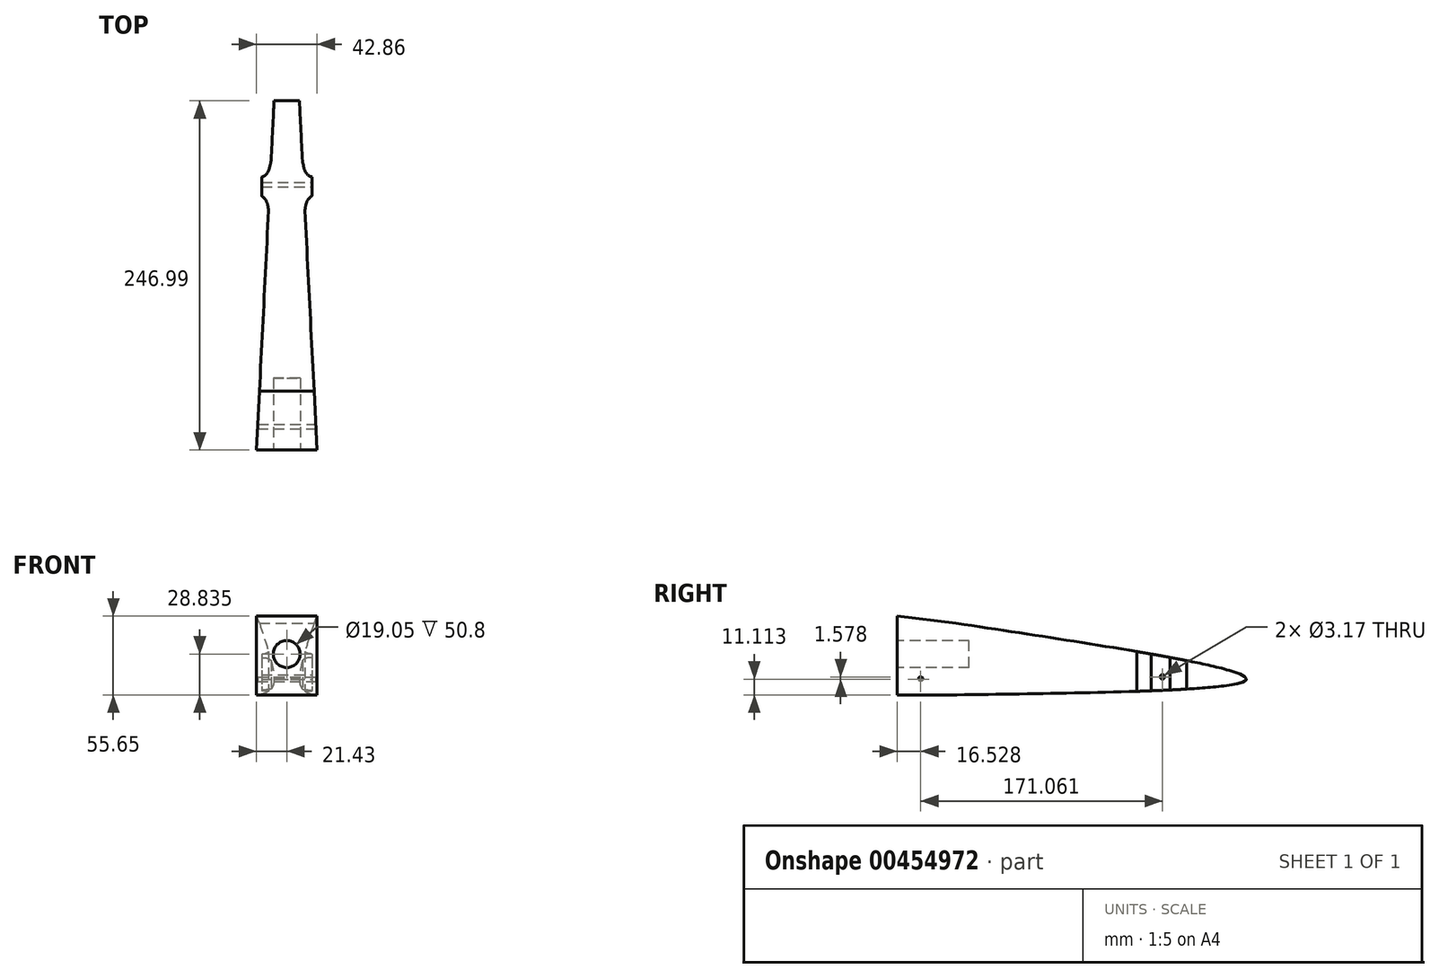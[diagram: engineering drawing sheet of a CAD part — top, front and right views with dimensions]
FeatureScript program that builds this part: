
annotation { "Feature Type Name" : "Feature", "Feature Type Description" : "" }
export const myFeature = defineFeature(function(context is Context, id is Id, definition is map)
    precondition{}
    {
        {
            var Q0;
            Q0=qCreatedBy(makeId("Right.planeOp"),FACE);
            var sketch = newSketch(context, id + "F0", { "sketchPlane" : qUnion([Q0])});
            skLineSegment(sketch, "E0", {"start": v(-152.4, 0) * mm, "end": v(152.4, 0) * mm});
            skLineSegment(sketch, "E1", {"start": v(-152.4, 0) * mm, "end": v(-152.4, 69.85) * mm});
            skLineSegment(sketch, "E2", {"start": v(152.4, 0) * mm, "end": v(152.4, 19.05) * mm});
            skLineSegment(sketch, "E3", {"start": v(152.4, 19.05) * mm, "end": v(-152.4, 69.85) * mm});
            skPoint(sketch, "E4.endSnap0", {"position": v(-152.4, 34.93) * mm});
            skLineSegment(sketch, "E5.0", {"start": v(-95.25, 50.8) * mm, "end": v(-152.4, 50.8) * mm, "construction": true});
            skLineSegment(sketch, "E5.1", {"start": v(-95.25, 50.8) * mm, "end": v(-95.25, 19.05) * mm, "construction": true});
            skLineSegment(sketch, "E5.2", {"start": v(-95.25, 19.05) * mm, "end": v(-152.4, 19.05) * mm, "construction": true});
            skSolve(sketch);
        }
        {
            var Q0;
            Q0=makeQuery(id+"F0.imprint","IMPRINT",FACE,{"disambiguationData":[TD([[makeQuery(id+"F0.imprint","IMPRINT",EDGE,{"derivedFrom":sQuery(id+"F0.wireOp",EDGE,"E0")}),1.0]])]});
            extrude(context, id + "F1", {"entities" : qUnion([Q0]), "depth" : 42.86 * mm, "symmetric" : true});
        }
        {
            var Q0;
            Q0=makeQuery(id+"F1.opExtrude","SWEPT_FACE",FACE,{"disambiguationData":[OSD([sQuery(id+"F0.wireOp",EDGE,"E1")])]});
            var sketch = newSketch(context, id + "F2", { "sketchPlane" : qUnion([Q0])});
            skLineSegment(sketch, "E6", {"start": v(21.43, 34.93) * mm, "end": v(0, 34.93) * mm, "construction": true});
            skCircle(sketch, "E7", {"center": v(0, 34.93) * mm, "radius": 9.53 * mm});
            skSolve(sketch);
        }
        {
            var Q0;
            Q0=makeQuery(id+"F2.imprint","IMPRINT",FACE,{"disambiguationData":[TD([[makeQuery(id+"F2.imprint","IMPRINT",EDGE,{"derivedFrom":sQuery(id+"F2.wireOp",EDGE,"E7")}),1.0]])]});
            var Q1;
            Q1=sQuery(id+"F2.wireOp",EDGE,"E7");
            extrude(context, id + "F3", {"entities" : qUnion([Q0]), "operationType" : NewBodyOperationType.REMOVE, "surfaceEntities" : qUnion([Q1]), "oppositeDirection" : true, "depth" : 50.8 * mm});
        }
        {
            var Q0;
            Q0=makeQuery(id+"F1.opExtrude","CAP_FACE",FACE,{"disambiguationData":[OSD([sQuery(id+"F0.wireOp",EDGE,"E0"),sQuery(id+"F0.wireOp",EDGE,"E1"),sQuery(id+"F0.wireOp",EDGE,"E2"),sQuery(id+"F0.wireOp",EDGE,"E3")])],"isStart":false});
            var sketch = newSketch(context, id + "F4", { "sketchPlane" : qUnion([Q0])});
            skLineSegment(sketch, "E8", {"start": v(-152.4, 34.93) * mm, "end": v(-152.4, 44.45) * mm, "construction": true});
            skLineSegment(sketch, "E9.0", {"start": v(-95.25, 19.05) * mm, "end": v(-152.4, 19.05) * mm, "construction": true});
            skLineSegment(sketch, "E9.1", {"start": v(-95.25, 50.8) * mm, "end": v(-95.25, 19.05) * mm, "construction": true});
            skLineSegment(sketch, "E9.2", {"start": v(-152.4, 50.8) * mm, "end": v(-95.25, 50.8) * mm, "construction": true});
            skLineSegment(sketch, "E10", {"start": v(57.15, 0) * mm, "end": v(57.15, 34.93) * mm, "construction": true});
            skLineSegment(sketch, "E11", {"start": v(-152.4, 44.45) * mm, "end": v(-101.6, 44.45) * mm, "construction": true});
            skLineSegment(sketch, "E12", {"start": v(-101.6, 44.45) * mm, "end": v(-101.6, 25.4) * mm, "construction": true});
            skLineSegment(sketch, "E13", {"start": v(-101.6, 25.4) * mm, "end": v(-152.4, 25.4) * mm, "construction": true});
            skFitSpline(sketch, "E14", {"points": [v(-110.78, 56.68) * mm, v(94.6, 17.22) * mm, v(-110.28, 6.1) * mm], "startDerivative": vector(614.92, -92.65) * mm, "endDerivative": vector(-615.87, -8.39) * mm});
            skLineSegment(sketch, "E15", {"start": v(-110.78, 56.68) * mm, "end": v(-152.4, 61.74) * mm});
            skLineSegment(sketch, "E16", {"start": v(-110.28, 6.1) * mm, "end": v(-152.4, 6.1) * mm});
            skCircle(sketch, "E17", {"center": v(-135.87, 17.2) * mm, "radius": 1.59 * mm});
            skCircle(sketch, "E18", {"center": v(35.19, 18.78) * mm, "radius": 1.59 * mm});
            skLineSegment(sketch, "E19", {"start": v(35.19, 18.78) * mm, "end": v(35.19, 9.26) * mm, "construction": true});
            skLineSegment(sketch, "E20", {"start": v(-135.9, 15.62) * mm, "end": v(-135.9, 6.1) * mm});
            skSolve(sketch);
        }
        {
            var Q0;
            Q0=makeQuery(id+"F1.opExtrude","SWEPT_FACE",FACE,{"disambiguationData":[OSD([sQuery(id+"F0.wireOp",EDGE,"E0")])]});
            var sketch = newSketch(context, id + "F5", { "sketchPlane" : qUnion([Q0])});
            skLineSegment(sketch, "E21", {"start": v(0, 152.4) * mm, "end": v(0, -27.28) * mm, "construction": true});
            skLineSegment(sketch, "E22", {"start": v(15.88, 152.4) * mm, "end": v(15.88, 95.25) * mm, "construction": true});
            skLineSegment(sketch, "E23", {"start": v(15.88, 95.25) * mm, "end": v(-15.87, 95.25) * mm, "construction": true});
            skLineSegment(sketch, "E24", {"start": v(-15.87, 95.25) * mm, "end": v(-15.87, 152.4) * mm, "construction": true});
            skLineSegment(sketch, "E25", {"start": v(0, 152.4) * mm, "end": v(-9.53, 152.4) * mm, "construction": true});
            skLineSegment(sketch, "E26", {"start": v(-9.53, 152.4) * mm, "end": v(-9.53, 101.6) * mm, "construction": true});
            skLineSegment(sketch, "E27", {"start": v(-9.52, 101.6) * mm, "end": v(9.53, 101.6) * mm, "construction": true});
            skLineSegment(sketch, "E28", {"start": v(9.53, 101.6) * mm, "end": v(9.53, 152.4) * mm, "construction": true});
            skLineSegment(sketch, "E29", {"start": v(-21.43, 152.4) * mm, "end": v(-21.43, -94.59) * mm, "construction": true});
            skLineSegment(sketch, "E30", {"start": v(-21.43, 152.4) * mm, "end": v(-12.86, -17.12) * mm});
            skLineSegment(sketch, "E31.MirrorCS", {"start": v(21.43, 152.4) * mm, "end": v(12.86, -17.12) * mm});
            skLineSegment(sketch, "E32", {"start": v(8.94, -94.59) * mm, "end": v(-8.94, -94.59) * mm});
            skLineSegment(sketch, "E33.right", {"start": v(17.78, -27.28) * mm, "end": v(17.78, -40.67) * mm});
            skFitSpline(sketch, "E34", {"points": [v(17.78, -40.67) * mm, v(14, -43.13) * mm, v(11.09, -52.15) * mm], "startDerivative": vector(-10.15, -4.14) * mm, "endDerivative": vector(-3.63, -17.97) * mm});
            skFitSpline(sketch, "E35", {"points": [v(17.78, -27.28) * mm, v(14.54, -23.86) * mm, v(12.86, -17.12) * mm], "startDerivative": vector(-8.1, 6.5) * mm, "endDerivative": vector(-1.95, 13.58) * mm});
            skFitSpline(sketch, "E36.MirrorCS", {"points": [v(-17.78, -27.28) * mm, v(-14.54, -23.86) * mm, v(-12.86, -17.12) * mm], "startDerivative": vector(8.1, 6.5) * mm, "endDerivative": vector(1.95, 13.58) * mm});
            skLineSegment(sketch, "E37.MirrorCS", {"start": v(-17.78, -27.28) * mm, "end": v(-17.78, -40.67) * mm});
            skFitSpline(sketch, "E38.MirrorCS", {"points": [v(-17.78, -40.67) * mm, v(-14, -43.13) * mm, v(-11.09, -52.15) * mm], "startDerivative": vector(10.15, -4.14) * mm, "endDerivative": vector(3.63, -17.97) * mm});
            skLineSegment(sketch, "E39.trimOffspring", {"start": v(11.09, -52.15) * mm, "end": v(8.94, -94.59) * mm});
            skLineSegment(sketch, "E40.trimOffspring", {"start": v(-11.09, -52.15) * mm, "end": v(-8.94, -94.59) * mm});
            skLineSegment(sketch, "E41.trimOffspring", {"start": v(0, -40.67) * mm, "end": v(0, -152.4) * mm, "construction": true});
            skSolve(sketch);
        }
        {
            var Q0;
            Q0=makeQuery(id+"F4.imprint","IMPRINT",FACE,{"disambiguationData":[TD([[makeQuery(id+"F4.imprint","IMPRINT",EDGE,{"derivedFrom":sQuery(id+"F4.wireOp",EDGE,"E14")}),-1.0]])]});
            extrude(context, id + "F6", {"entities" : qUnion([Q0]), "operationType" : NewBodyOperationType.INTERSECT, "endBound" : BoundingType.THROUGH_ALL, "oppositeDirection" : true, "depth" : 25.4 * mm});
        }
        {
            var Q0;
            Q0=makeQuery(id+"F5.imprint","IMPRINT",FACE,{"disambiguationData":[TD([[makeQuery(id+"F5.imprint","IMPRINT",EDGE,{"derivedFrom":sQuery(id+"F5.wireOp",EDGE,"E30")}),1.0]])]});
            extrude(context, id + "F7", {"entities" : qUnion([Q0]), "operationType" : NewBodyOperationType.INTERSECT, "endBound" : BoundingType.THROUGH_ALL, "oppositeDirection" : true, "depth" : 25.4 * mm});
        }
    });
